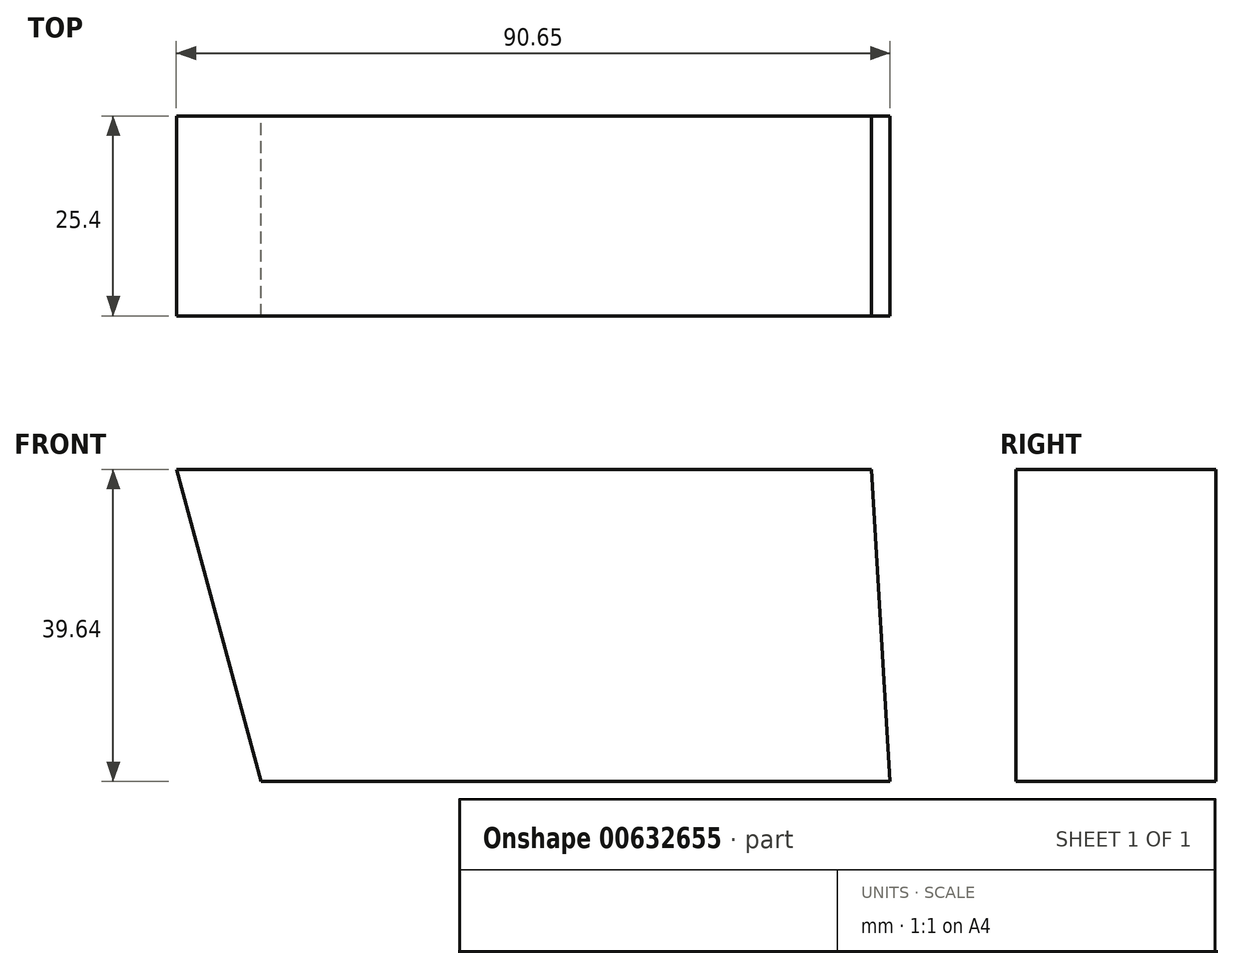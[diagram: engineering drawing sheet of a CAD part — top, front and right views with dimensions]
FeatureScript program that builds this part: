
annotation { "Feature Type Name" : "Feature", "Feature Type Description" : "" }
export const myFeature = defineFeature(function(context is Context, id is Id, definition is map)
    precondition{}
    {
        {
            var Q0;
            Q0=qCreatedBy(makeId("Front.planeOp"),FACE);
            var sketch = newSketch(context, id + "F0", { "sketchPlane" : qUnion([Q0])});
            skLineSegment(sketch, "E0", {"start": v(-49.99, 21.86) * mm, "end": v(38.33, 21.86) * mm});
            skLineSegment(sketch, "E1", {"start": v(38.33, 21.86) * mm, "end": v(40.66, -17.78) * mm});
            skLineSegment(sketch, "E2", {"start": v(40.66, -17.78) * mm, "end": v(-39.2, -17.78) * mm});
            skLineSegment(sketch, "E3", {"start": v(-39.2, -17.78) * mm, "end": v(-49.99, 21.86) * mm});
            skSolve(sketch);
        }
        {
            var Q0;
            Q0=makeQuery(id+"F0.imprint","IMPRINT",FACE,{"disambiguationData":[TD([[makeQuery(id+"F0.imprint","IMPRINT",EDGE,{"derivedFrom":sQuery(id+"F0.wireOp",EDGE,"E0")}),-1.0]])]});
            extrude(context, id + "F1", {"entities" : qUnion([Q0]), "depth" : 25.4 * mm, "offsetDistance" : 25.4 * mm});
        }
    });
